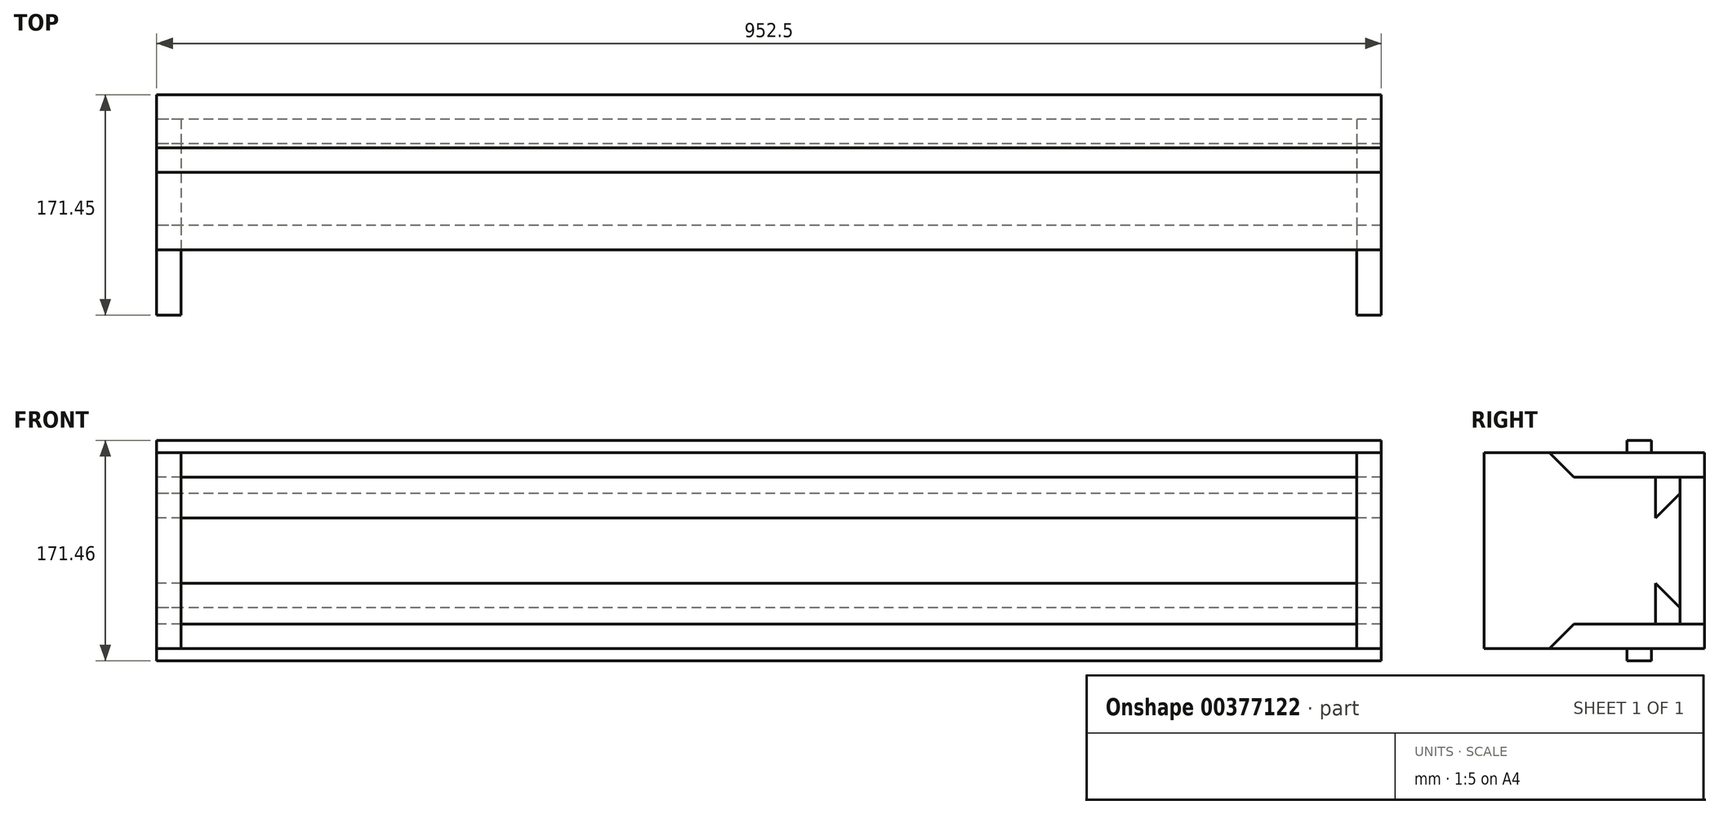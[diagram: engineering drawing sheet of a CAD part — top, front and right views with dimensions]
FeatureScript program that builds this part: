
annotation { "Feature Type Name" : "Feature", "Feature Type Description" : "" }
export const myFeature = defineFeature(function(context is Context, id is Id, definition is map)
    precondition{}
    {
        {
            var Q0;
            Q0=qCreatedBy(makeId("Right.planeOp"),FACE);
            var sketch = newSketch(context, id + "F0", { "sketchPlane" : qUnion([Q0])});
            skLineSegment(sketch, "E0", {"start": v(0, 0) * mm, "end": v(50.8, 0) * mm});
            skLineSegment(sketch, "E1", {"start": v(50.8, 0) * mm, "end": v(69.85, 19.05) * mm});
            skLineSegment(sketch, "E2", {"start": v(69.85, 19.05) * mm, "end": v(133.35, 19.05) * mm});
            skLineSegment(sketch, "E3", {"start": v(133.35, 50.8) * mm, "end": v(152.4, 31.75) * mm});
            skLineSegment(sketch, "E4", {"start": v(152.4, 120.65) * mm, "end": v(133.35, 101.6) * mm});
            skLineSegment(sketch, "E5", {"start": v(133.35, 101.6) * mm, "end": v(133.35, 133.35) * mm});
            skLineSegment(sketch, "E6", {"start": v(133.35, 133.35) * mm, "end": v(69.85, 133.35) * mm});
            skLineSegment(sketch, "E7", {"start": v(69.85, 133.35) * mm, "end": v(50.8, 152.4) * mm});
            skLineSegment(sketch, "E8", {"start": v(50.8, 152.4) * mm, "end": v(0, 152.4) * mm});
            skLineSegment(sketch, "E9", {"start": v(0, 152.4) * mm, "end": v(0, 0) * mm});
            skLineSegment(sketch, "E10", {"start": v(152.4, 120.65) * mm, "end": v(152.4, 31.75) * mm});
            skLineSegment(sketch, "E11", {"start": v(133.35, 50.8) * mm, "end": v(133.35, 19.05) * mm});
            skSolve(sketch);
        }
        {
            var Q0;
            Q0 = qSketchRegion(id + "F0", true);
            extrude(context, id + "F1", {"entities" : qUnion([Q0]), "depth" : 19.05 * mm});
        }
        {
            var Q0;
            Q0=qCreatedBy(makeId("Right.planeOp"),FACE);
            var sketch = newSketch(context, id + "F2", { "sketchPlane" : qUnion([Q0])});
            skLineSegment(sketch, "E12", {"start": v(50.8, 0) * mm, "end": v(69.85, 19.05) * mm});
            skLineSegment(sketch, "E13", {"start": v(69.85, 19.05) * mm, "end": v(171.45, 19.05) * mm});
            skLineSegment(sketch, "E14", {"start": v(171.45, 19.05) * mm, "end": v(171.45, 0) * mm});
            skLineSegment(sketch, "E15", {"start": v(171.45, 0) * mm, "end": v(50.8, 0) * mm});
            skLineSegment(sketch, "E16", {"start": v(50.8, 152.4) * mm, "end": v(69.85, 133.35) * mm});
            skLineSegment(sketch, "E17", {"start": v(69.85, 133.35) * mm, "end": v(171.45, 133.35) * mm});
            skLineSegment(sketch, "E18", {"start": v(50.8, 152.4) * mm, "end": v(171.45, 152.4) * mm});
            skLineSegment(sketch, "E19", {"start": v(171.45, 152.4) * mm, "end": v(171.45, 133.35) * mm});
            skSolve(sketch);
        }
        {
            var Q0;
            Q0 = qSketchRegion(id + "F2", true);
            extrude(context, id + "F3", {"entities" : qUnion([Q0]), "depth" : 952.5 * mm});
        }
        {
            var Q0;
            Q0=qCreatedBy(makeId("Right.planeOp"),FACE);
            var sketch = newSketch(context, id + "F4", { "sketchPlane" : qUnion([Q0])});
            skLineSegment(sketch, "E20.bottom", {"start": v(171.45, 19.05) * mm, "end": v(152.4, 19.05) * mm});
            skLineSegment(sketch, "E20.top", {"start": v(171.45, 133.35) * mm, "end": v(152.4, 133.35) * mm});
            skLineSegment(sketch, "E20.left", {"start": v(171.45, 19.05) * mm, "end": v(171.45, 133.35) * mm});
            skLineSegment(sketch, "E20.right", {"start": v(152.4, 19.05) * mm, "end": v(152.4, 133.35) * mm});
            skSolve(sketch);
        }
        {
            var Q0;
            Q0 = qSketchRegion(id + "F4", true);
            extrude(context, id + "F5", {"entities" : qUnion([Q0]), "depth" : 952.5 * mm});
        }
        {
            var Q0;
            Q0=qCreatedBy(makeId("Right.planeOp"),FACE);
            var sketch = newSketch(context, id + "F6", { "sketchPlane" : qUnion([Q0])});
            skLineSegment(sketch, "E21", {"start": v(152.35, 133.35) * mm, "end": v(133.3, 133.35) * mm});
            skLineSegment(sketch, "E22", {"start": v(133.3, 133.35) * mm, "end": v(133.3, 101.6) * mm});
            skLineSegment(sketch, "E23", {"start": v(133.3, 101.6) * mm, "end": v(152.35, 120.65) * mm});
            skLineSegment(sketch, "E24", {"start": v(152.35, 120.65) * mm, "end": v(152.35, 133.35) * mm});
            skLineSegment(sketch, "E25", {"start": v(152.35, 19.05) * mm, "end": v(152.35, 31.75) * mm});
            skLineSegment(sketch, "E26", {"start": v(152.35, 31.75) * mm, "end": v(133.3, 50.8) * mm});
            skLineSegment(sketch, "E27", {"start": v(133.3, 50.8) * mm, "end": v(133.3, 19.05) * mm});
            skLineSegment(sketch, "E28", {"start": v(133.3, 19.05) * mm, "end": v(152.35, 19.05) * mm});
            skSolve(sketch);
        }
        {
            var Q0;
            Q0 = qSketchRegion(id + "F6", true);
            extrude(context, id + "F7", {"entities" : qUnion([Q0]), "depth" : 952.5 * mm});
        }
        {
            var Q0;
            Q0=makeQuery(id+"F1.opExtrude","SWEPT_BODY",BODY,{"disambiguationData":[OSD([sQuery(id+"F0.wireOp",EDGE,"E0"),sQuery(id+"F0.wireOp",EDGE,"E1"),sQuery(id+"F0.wireOp",EDGE,"E2"),sQuery(id+"F0.wireOp",EDGE,"E3"),sQuery(id+"F0.wireOp",EDGE,"E4"),sQuery(id+"F0.wireOp",EDGE,"E5"),sQuery(id+"F0.wireOp",EDGE,"E6"),sQuery(id+"F0.wireOp",EDGE,"E7"),sQuery(id+"F0.wireOp",EDGE,"E8"),sQuery(id+"F0.wireOp",EDGE,"E9"),sQuery(id+"F0.wireOp",EDGE,"E10"),sQuery(id+"F0.wireOp",EDGE,"E11")])]});
            transform(context, id + "F8", {"entities" : qUnion([Q0]), "transformType" : TransformType.TRANSLATION_3D, "dx" : 933.45 * mm, "dy" : 0 * mm, "dz" : 0 * mm, "makeCopy" : true});
        }
        {
            var Q0;
            Q0=qCreatedBy(makeId("Right.planeOp"),FACE);
            var sketch = newSketch(context, id + "F9", { "sketchPlane" : qUnion([Q0])});
            skLineSegment(sketch, "E29.bottom", {"start": v(111.13, 0) * mm, "end": v(130.18, 0) * mm});
            skLineSegment(sketch, "E29.top", {"start": v(111.13, -9.52) * mm, "end": v(130.18, -9.52) * mm});
            skLineSegment(sketch, "E29.left", {"start": v(111.13, 0) * mm, "end": v(111.13, -9.52) * mm});
            skLineSegment(sketch, "E29.right", {"start": v(130.18, 0) * mm, "end": v(130.18, -9.53) * mm});
            skLineSegment(sketch, "E30.bottom", {"start": v(111.13, 161.93) * mm, "end": v(130.18, 161.93) * mm});
            skLineSegment(sketch, "E30.top", {"start": v(111.13, 152.4) * mm, "end": v(130.18, 152.4) * mm});
            skLineSegment(sketch, "E30.left", {"start": v(111.13, 161.93) * mm, "end": v(111.13, 152.4) * mm});
            skLineSegment(sketch, "E30.right", {"start": v(130.18, 161.93) * mm, "end": v(130.18, 152.4) * mm});
            skSolve(sketch);
        }
        {
            var Q0;
            Q0 = qSketchRegion(id + "F9", true);
            extrude(context, id + "F10", {"entities" : qUnion([Q0]), "depth" : 952.5 * mm});
        }
    });
